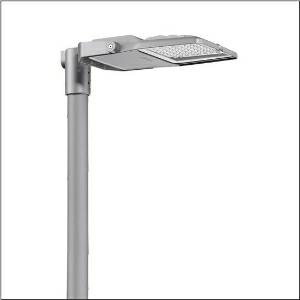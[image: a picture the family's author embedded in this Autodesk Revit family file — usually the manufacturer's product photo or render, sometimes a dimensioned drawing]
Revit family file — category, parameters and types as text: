
# Revit family: floodlight_fl_21_mini___pl61_5xa7776b2c3a_9e12
name_source: partatom
category: Lighting Fixtures
units: mm (PartAtom-declared; Revit-internal decimal feet)

## family parameters
Cut with Voids When Loaded = No
Host = Face
Light Source = No
Part Type = Normal
Room Calculation Point = No
Round Connector Dimension = Use Diameter
Shared = No

## types (1)
- --- (1 x LED, 6110 lm, 45.7 W, 3000K)
    Apparent Load = 46 VA
    CIE Flux Codes = 33 65 98 100 100
    Color Rendering = 70
    Color Temperature = 3000K
    Default Elevation = 1800 mm
    Description = Floodlight FL 21 mini, floodlight, primary light control with lens, of PMMA, primary optical cover: protective disc, of toughened safety glass, transparent, light distribution: PL61, light emission: direct distribution, installation type: surface-mounted, LED, High Power LED, rated luminous flux: 6.110lm, luminous efficacy: 134lm/W, light colour: 730, colour temperature: 3000K, control gear: Smart Interface (Zhaga), control: flexible luminous flux parameterisation, time-dependent luminous flux control, constant luminous flux control, overheat protection, pre-setting: logarithmic dimming characteristic, with terminal, 6-pole, mains connection: 220..240V, AC, 50/60Hz, start of lifetime: 46W, end of service life: 48W, reduction: 22W, luminaire housing, of diecast aluminium, powder-coated, Siteco® metallic grey (DB 702S), corrosivity category C5 mid according to DIN EN ISO 12944, suitable for swimming pools, chlorine-resistant, sealing non-destructively replaceable, please order mast flange separately, mast bracket, of steel, galvanised, powder-coated, Siteco® metallic grey (DB 702S), Smart Interface below and above, protection rating (complete): IP66, insulation class (complete): insulation class II (safety insulation), certification: CE, ENEC, VDE, protection symbol: D, impact resistance: IK08, permissible operating ambient temperature: -40..+40°C, permissible operating ambient temperature for outdoor applications: -40..+50°C, standard: DIN EN 12944, LABS conformity tested according to VDMA 24364:2018-05, packaging unit: 1 piece

Light Distribution: PL61
    Height = 70 mm
    Lamp = 1 x LED
    Lamp Light Flux = 6110 lm
    Lamp Power = 45.7 W
    Lamp count = 1
    Length = 485 mm
    Luminous efficacy = 134 lm/W
    Manufacturer = Siteco
    ModVariant = No
    Model = 5XA7776B2C3A
    Number of Poles = 1
    OnlyDefault = Yes
    Power Factor = 1
    Product Name = Floodlight FL 21 mini | PL61
    Product group = floodlight | pylon annexe
    ProductGroupID = 6200
    Protection Class = Protection class II
    Protection Degree = IP 66
    RLX_Detail_Level = 1
    RLX_Emergency_Light_Flux = 0 lm
    RLX_Emergency_Type = 0
    RLX_Emergency_Type_DB = No
    RlxData = <blob elided: 101189 chars, md5=07d373d3>
    Socket = socket
    Standby Power = 0 W
    System Light Flux = 6110 lm
    System Power = 46 W
    Type Comments = factory setting: luminous flux: 100 % | dim-lin: 254 | 463 mA
    Type Image = l_1007125.jpg
    URL = http://relux.com
    VarID = @adj_172126
    Voltage = 0 V
    Weight = 0.00 kg
    Width = 337 mm

## geometry (parser evidence)
native form markers: Blend x4, Sweep x13
no freeform markers — native parametric forms only
